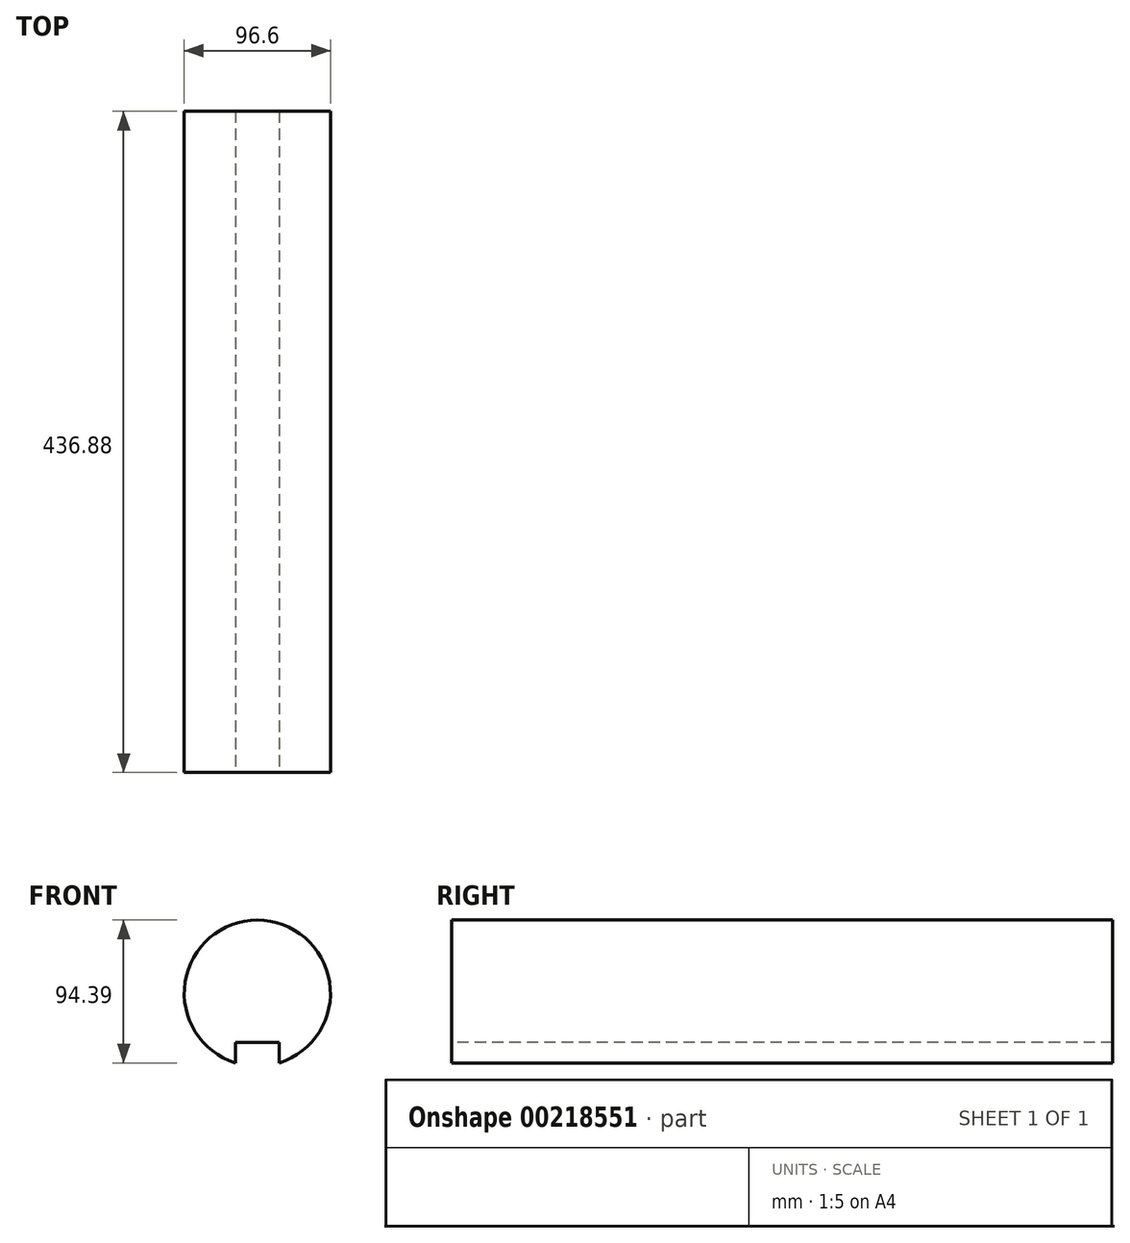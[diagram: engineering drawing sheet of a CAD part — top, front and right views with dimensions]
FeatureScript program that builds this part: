
annotation { "Feature Type Name" : "Feature", "Feature Type Description" : "" }
export const myFeature = defineFeature(function(context is Context, id is Id, definition is map)
    precondition{}
    {
        {
            var Q0;
            Q0=qCreatedBy(makeId("Front.planeOp"),FACE);
            var sketch = newSketch(context, id + "F0", { "sketchPlane" : qUnion([Q0])});
            skArc(sketch, "E0", {"start": v(14.43, -46.1) * mm, "mid": v(0, 48.3) * mm, "end": v(-14.43, -46.1) * mm});
            skLineSegment(sketch, "E1.top", {"start": v(-14.43, -32.42) * mm, "end": v(14.43, -32.42) * mm});
            skLineSegment(sketch, "E1.left", {"start": v(-14.43, -46.1) * mm, "end": v(-14.43, -32.42) * mm});
            skLineSegment(sketch, "E1.right", {"start": v(14.43, -46.1) * mm, "end": v(14.43, -32.42) * mm});
            skPoint(sketch, "E2", {"position": v(0, -32.42) * mm});
            skSolve(sketch);
        }
        {
            var Q0;
            Q0 = qSketchRegion(id + "F0", true);
            extrude(context, id + "F1", {"entities" : qUnion([Q0]), "oppositeDirection" : true, "depth" : 436.88 * mm});
        }
    });
